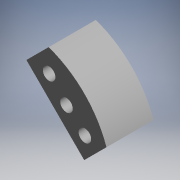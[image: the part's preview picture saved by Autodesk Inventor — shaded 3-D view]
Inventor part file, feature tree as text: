
AUTODESK INVENTOR PART (.ipt)
format: ipt  version: 2019.4 (Build 234330000, 330)  size: 106,496 bytes
history: native  units: mm
features: reference x6, other x3, extrude x1, sketch x1
ambient origin geometry x8: Origin, YZ Plane, XZ Plane, XY Plane, X Axis, Y Axis, Z Axis, Center Point
bodies: Solid1 (feature_tree)
feature tree (11):
  extrude  "Extrusion1"  Depth=6.5mm
  sketch  "Sketch1"  dims[d0=2.5mm d1=6.5mm d2=3.75mm d3=0.0mm]
  reference  "Reference1"
  reference  "Reference2"
  reference  "Reference3"
  reference  "Reference4"
  reference  "Reference5"
  reference  "Reference6"
  parser-record x1  (decoder bookkeeping rows leaked as tree rows — omitted from the tree; the rows remain in map.json)
  other  "motor_core.iam"
  other  "motor_body:1"
note: 1 file-system path scrubbed to <path> (originals preserved in map.json)
